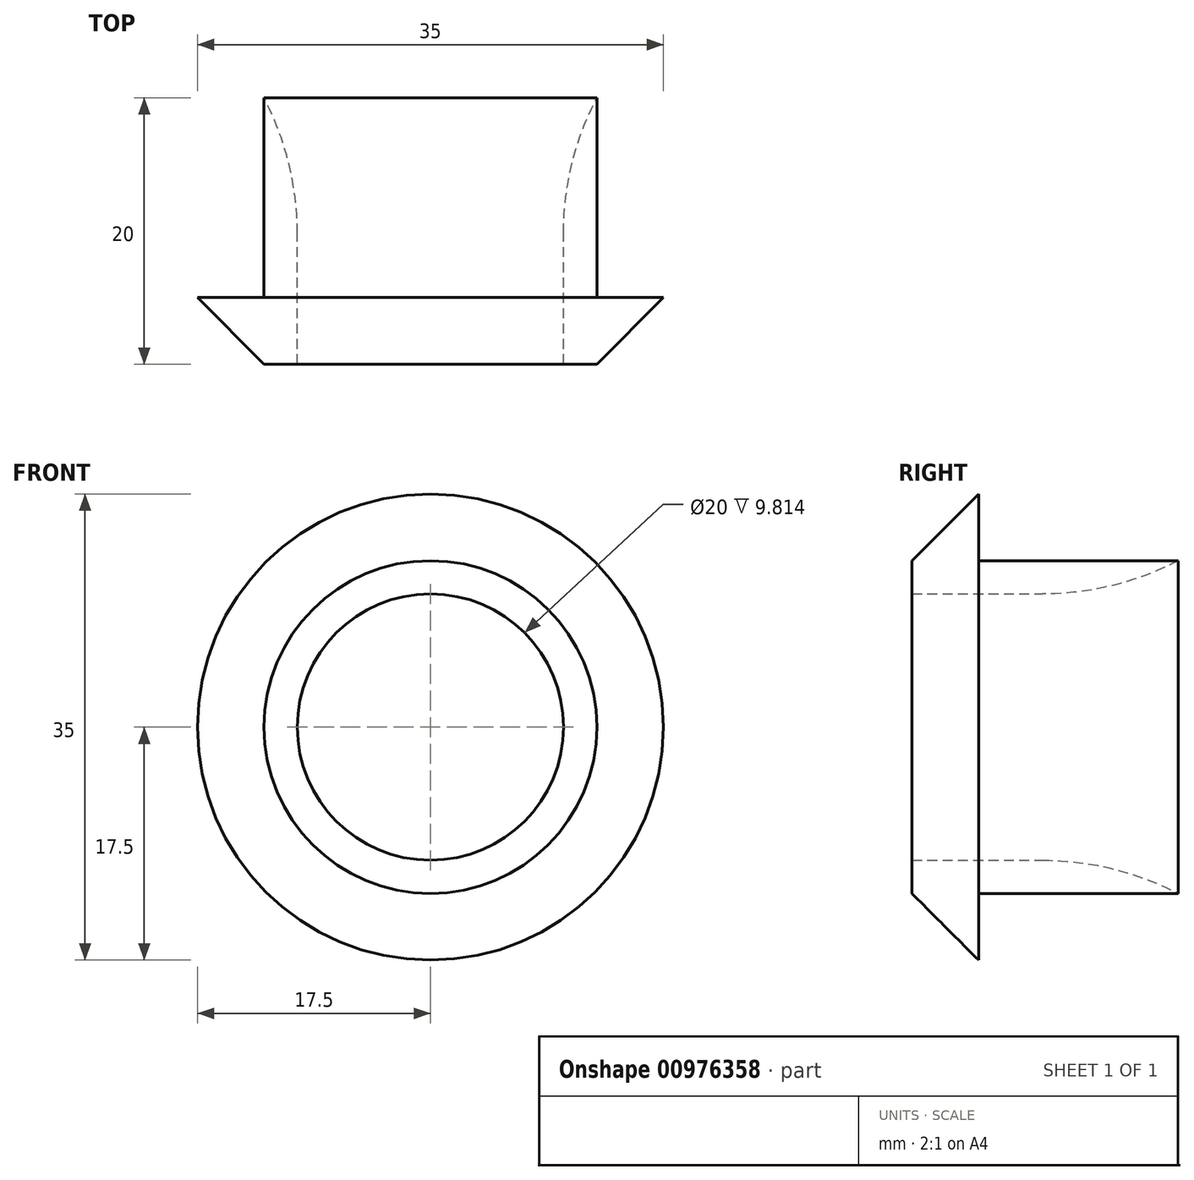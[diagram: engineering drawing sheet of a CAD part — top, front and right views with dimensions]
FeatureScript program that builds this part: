
annotation { "Feature Type Name" : "Feature", "Feature Type Description" : "" }
export const myFeature = defineFeature(function(context is Context, id is Id, definition is map)
    precondition{}
    {
        {
            var Q0;
            Q0=qCreatedBy(makeId("Front.planeOp"),FACE);
            var sketch = newSketch(context, id + "F0", { "sketchPlane" : qUnion([Q0])});
            skCircle(sketch, "E0", {"center": v(0, 0) * mm, "radius": 10 * mm});
            skCircle(sketch, "E1", {"center": v(0, 0) * mm, "radius": 12.5 * mm});
            skCircle(sketch, "E2", {"center": v(0, 0) * mm, "radius": 17.5 * mm});
            skSolve(sketch);
        }
        {
            var Q0;
            Q0=makeQuery(id+"F0.imprint","IMPRINT",FACE,{"disambiguationData":[TD([[makeQuery(id+"F0.imprint","IMPRINT",EDGE,{"derivedFrom":sQuery(id+"F0.wireOp",EDGE,"E0")}),-1.0]])]});
            var Q1;
            Q1=makeQuery(id+"F0.imprint","IMPRINT",FACE,{"disambiguationData":[TD([[makeQuery(id+"F0.imprint","IMPRINT",EDGE,{"derivedFrom":sQuery(id+"F0.wireOp",EDGE,"E1")}),-1.0]])]});
            extrude(context, id + "F1", {"entities" : qUnion([Q0, Q1]), "depth" : 5 * mm, "offsetDistance" : 25 * mm});
        }
        {
            var Q0;
            Q0=makeQuery(id+"F0.imprint","IMPRINT",FACE,{"disambiguationData":[TD([[makeQuery(id+"F0.imprint","IMPRINT",EDGE,{"derivedFrom":sQuery(id+"F0.wireOp",EDGE,"E0")}),-1.0]])]});
            extrude(context, id + "F2", {"entities" : qUnion([Q0]), "operationType" : NewBodyOperationType.ADD, "oppositeDirection" : true, "depth" : 15 * mm, "offsetDistance" : 25 * mm});
        }
        {
            var Q0;
            Q0=makeQuery(id+"F2.opExtrude","CAP_EDGE",EDGE,{"disambiguationData":[OSD([sQuery(id+"F0.wireOp",EDGE,"E0")])],"isStart":false});
            fillet(context, id + "F3", {"entities" : qUnion([Q0]), "radius" : 22 * mm, "tangentPropagation" : true, "allowEdgeOverflow" : false});
        }
        {
            var Q0;
            Q0=makeQuery(id+"F1.opExtrude","CAP_EDGE",EDGE,{"disambiguationData":[OSD([sQuery(id+"F0.wireOp",EDGE,"E2")])],"isStart":false});
            chamfer(context, id + "F4", {"entities" : qUnion([Q0]), "width" : 5 * mm, "tangentPropagation" : true});
        }
    });
